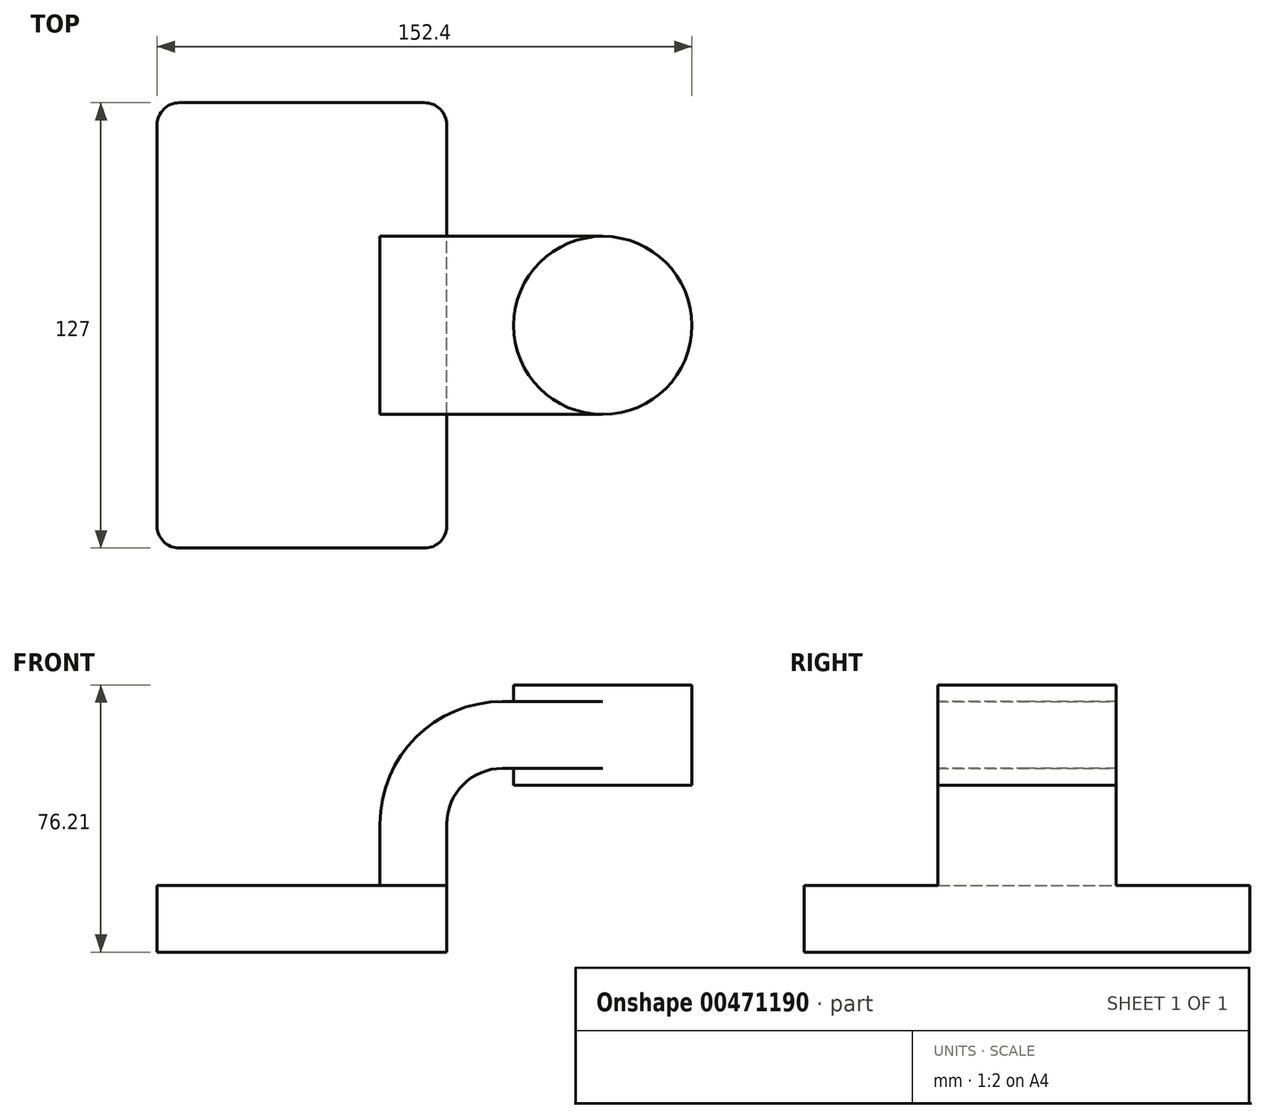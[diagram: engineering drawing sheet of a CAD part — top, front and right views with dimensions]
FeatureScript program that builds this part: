
annotation { "Feature Type Name" : "Feature", "Feature Type Description" : "" }
export const myFeature = defineFeature(function(context is Context, id is Id, definition is map)
    precondition{}
    {
        {
            var Q0;
            Q0=qCreatedBy(makeId("Front.planeOp"),FACE);
            var sketch = newSketch(context, id + "F0", { "sketchPlane" : qUnion([Q0])});
            skLineSegment(sketch, "E0.bottom", {"start": v(-41.28, 9.53) * mm, "end": v(41.27, 9.53) * mm});
            skLineSegment(sketch, "E0.top", {"start": v(-41.27, -9.52) * mm, "end": v(41.28, -9.52) * mm});
            skLineSegment(sketch, "E0.left", {"start": v(-41.28, 9.53) * mm, "end": v(-41.27, -9.52) * mm});
            skLineSegment(sketch, "E0.right", {"start": v(41.28, 9.53) * mm, "end": v(41.28, -9.52) * mm});
            skPoint(sketch, "E0.middle", {"position": v(0, 0) * mm});
            skLineSegment(sketch, "E1.bottom", {"start": v(60.32, 66.68) * mm, "end": v(111.12, 66.68) * mm});
            skLineSegment(sketch, "E1.top", {"start": v(60.33, 38.1) * mm, "end": v(111.12, 38.1) * mm});
            skLineSegment(sketch, "E1.left", {"start": v(60.32, 66.67) * mm, "end": v(60.33, 38.1) * mm});
            skLineSegment(sketch, "E1.right", {"start": v(111.12, 66.67) * mm, "end": v(111.12, 38.1) * mm});
            skPoint(sketch, "E1.middle", {"position": v(85.72, 52.39) * mm});
            skLineSegment(sketch, "E2", {"start": v(41.27, 9.53) * mm, "end": v(41.27, 27) * mm});
            skArc(sketch, "E3", {"start": v(41.27, 27) * mm, "mid": v(45.92, 38.23) * mm, "end": v(57.15, 42.88) * mm});
            skArc(sketch, "E4.1", {"start": v(22.23, 27) * mm, "mid": v(32.45, 51.7) * mm, "end": v(57.15, 61.93) * mm});
            skLineSegment(sketch, "E4.2", {"start": v(22.22, 9.53) * mm, "end": v(22.22, 27) * mm});
            skLineSegment(sketch, "E5", {"start": v(85.72, 38.1) * mm, "end": v(85.72, 66.68) * mm});
            skFitSpline(sketch, "E6", {"points": [v(-41.28, 9.52) * mm, v(57.15, 61.93) * mm], "startDerivative": vector(1.38, 73.15) * mm, "endDerivative": vector(123.7, -26.38) * mm});
            skLineSegment(sketch, "E7", {"start": v(57.15, 61.93) * mm, "end": v(85.72, 61.93) * mm});
            skLineSegment(sketch, "E8", {"start": v(57.15, 42.88) * mm, "end": v(85.72, 42.88) * mm});
            skSolve(sketch);
        }
        {
            var Q0;
            {var subQ0=sQuery(id+"F0.wireOp",EDGE,"E7");var subQ1=sQuery(id+"F0.wireOp",EDGE,"E1.left");var subQ2=makeQuery(id+"F0.imprint","INTERSECT",VERTEX,{"derivedFrom":[subQ1,subQ0]});Q0=makeQuery(id+"F0.imprint","IMPRINT",FACE,{"disambiguationData":[TD([[makeQuery(id+"F0.imprint","IMPRINT",EDGE,{"disambiguationData":[TD([[subQ2,-1.0]])],"derivedFrom":subQ1}),1.0]])]});}
            var Q1;
            {var subQ1=sQuery(id+"F0.wireOp",EDGE,"E2");Q1=makeQuery(id+"F0.imprint","IMPRINT",FACE,{"disambiguationData":[TD([[makeQuery(id+"F0.imprint","IMPRINT",EDGE,{"derivedFrom":subQ1}),1.0]])]});}
            extrude(context, id + "F1", {"entities" : qUnion([Q0, Q1]), "endBound" : BoundingType.SYMMETRIC, "depth" : 50.8 * mm});
        }
        {
            var Q0;
            Q0=makeQuery(id+"F0.imprint","IMPRINT",FACE,{"disambiguationData":[TD([[makeQuery(id+"F0.imprint","IMPRINT",EDGE,{"derivedFrom":sQuery(id+"F0.wireOp",EDGE,"E0.top")}),1.0]])]});
            extrude(context, id + "F2", {"entities" : qUnion([Q0]), "operationType" : NewBodyOperationType.ADD, "endBound" : BoundingType.SYMMETRIC, "depth" : 127 * mm});
        }
        {
            var Q0;
            Q0=makeQuery(id+"F0.imprint","IMPRINT",FACE,{"disambiguationData":[TD([[makeQuery(id+"F0.imprint","IMPRINT",EDGE,{"derivedFrom":sQuery(id+"F0.wireOp",EDGE,"E4.1")}),1.0]])]});
            extrude(context, id + "F3", {"entities" : qUnion([Q0]), "operationType" : NewBodyOperationType.ADD, "endBound" : BoundingType.SYMMETRIC, "depth" : 15.88 * mm});
        }
        {
            var Q0;
            {var subQ4=sQuery(id+"F0.wireOp",EDGE,"E1.right");Q0=makeQuery(id+"F0.imprint","IMPRINT",FACE,{"disambiguationData":[TD([[makeQuery(id+"F0.imprint","IMPRINT",EDGE,{"derivedFrom":subQ4}),-1.0]])]});}
            var Q1;
            Q1=sQuery(id+"F0.wireOp",EDGE,"E5");
            revolve(context, id + "F4", {"operationType" : NewBodyOperationType.ADD, "entities" : qUnion([Q0]), "axis" : qUnion([Q1]), "revolveType" : RevolveType.FULL});
        }
        {
            var Q0;
            Q0=makeQuery(id+"F2.opExtrude","CAP_EDGE",EDGE,{"disambiguationData":[OSD([sQuery(id+"F0.wireOp",EDGE,"E0.right")])],"isStart":false});
            var Q1;
            Q1=makeQuery(id+"F2.opExtrude","CAP_EDGE",EDGE,{"disambiguationData":[OSD([sQuery(id+"F0.wireOp",EDGE,"E0.left")])],"isStart":false});
            var Q2;
            Q2=makeQuery(id+"F2.opExtrude","CAP_EDGE",EDGE,{"disambiguationData":[OSD([sQuery(id+"F0.wireOp",EDGE,"E0.left")])],"isStart":true});
            var Q3;
            Q3=makeQuery(id+"F2.opExtrude","CAP_EDGE",EDGE,{"disambiguationData":[OSD([sQuery(id+"F0.wireOp",EDGE,"E0.right")])],"isStart":true});
            fillet(context, id + "F5", {"entities" : qUnion([Q0, Q1, Q2, Q3]), "radius" : 6.35 * mm, "tangentPropagation" : true, "allowEdgeOverflow" : false});
        }
    });
